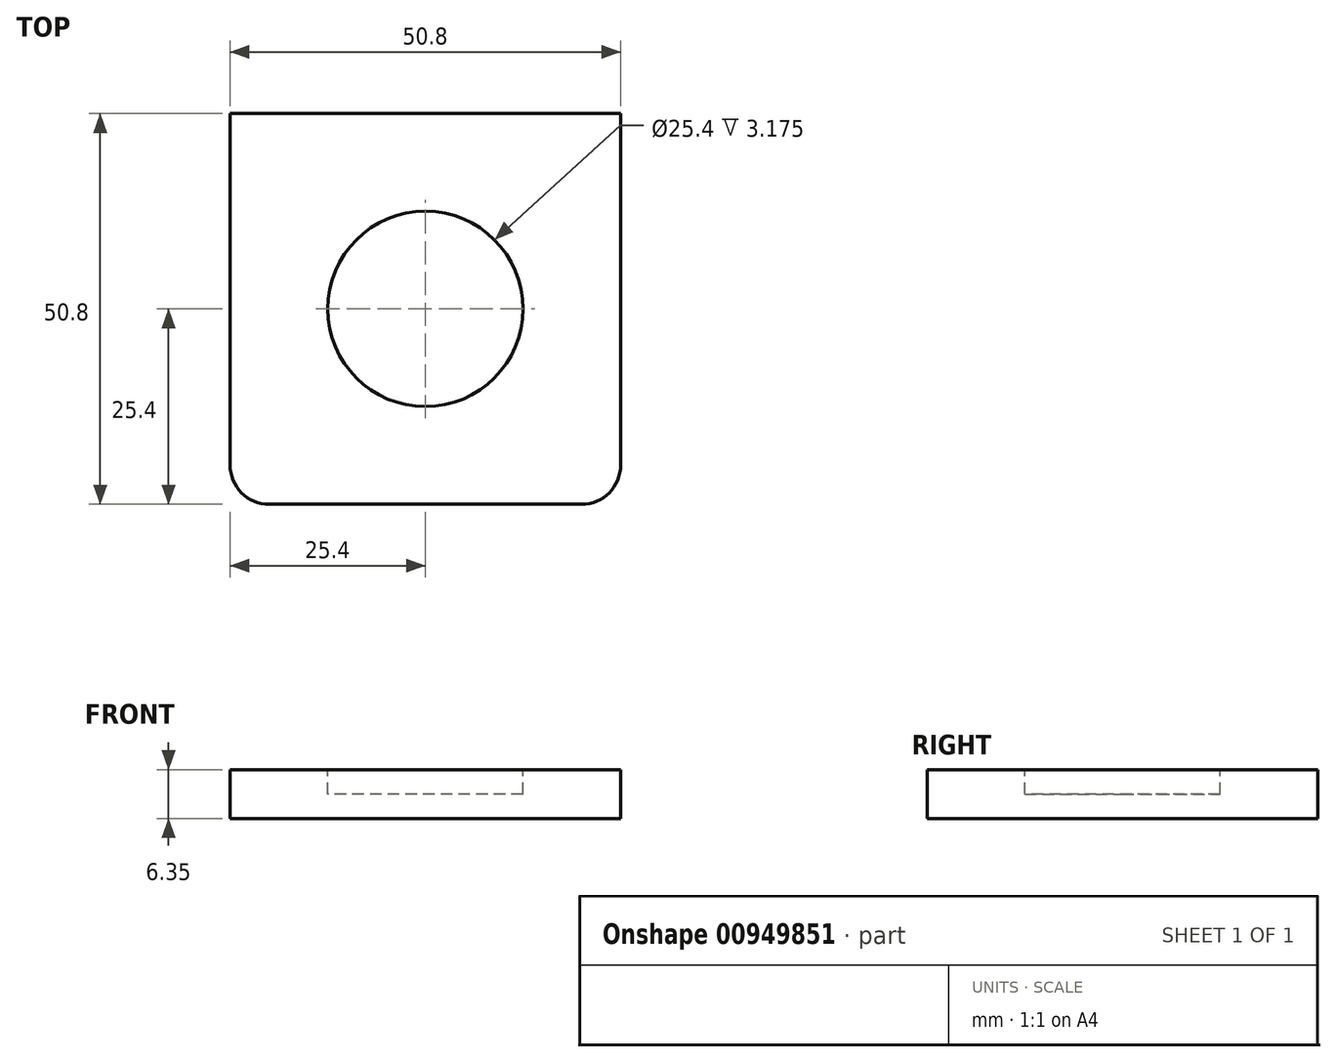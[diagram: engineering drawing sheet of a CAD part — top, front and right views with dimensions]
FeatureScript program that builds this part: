
annotation { "Feature Type Name" : "Feature", "Feature Type Description" : "" }
export const myFeature = defineFeature(function(context is Context, id is Id, definition is map)
    precondition{}
    {
        {
            var Q0;
            Q0=qCreatedBy(makeId("Top.planeOp"),FACE);
            var sketch = newSketch(context, id + "F0", { "sketchPlane" : qUnion([Q0])});
            skLineSegment(sketch, "E0.bottom", {"start": v(25.4, -25.4) * mm, "end": v(-25.4, -25.4) * mm});
            skLineSegment(sketch, "E0.top", {"start": v(25.4, 25.4) * mm, "end": v(-25.4, 25.4) * mm});
            skLineSegment(sketch, "E0.left", {"start": v(25.4, -25.4) * mm, "end": v(25.4, 25.4) * mm});
            skLineSegment(sketch, "E0.right", {"start": v(-25.4, -25.4) * mm, "end": v(-25.4, 25.4) * mm});
            skPoint(sketch, "E0.middle", {"position": v(0, 0) * mm});
            skSolve(sketch);
        }
        {
            var Q0;
            Q0=makeQuery(id+"F0.imprint","IMPRINT",FACE,{"disambiguationData":[TD([[makeQuery(id+"F0.imprint","IMPRINT",EDGE,{"derivedFrom":sQuery(id+"F0.wireOp",EDGE,"E0.bottom")}),-1.0]])]});
            extrude(context, id + "F1", {"entities" : qUnion([Q0]), "depth" : 6.35 * mm, "offsetDistance" : 25.4 * mm});
        }
        {
            var Q0;
            Q0=makeQuery(id+"F1.opExtrude","SWEPT_EDGE",EDGE,{"disambiguationData":[OSD([sQuery(id+"F0.wireOp",EDGE,"E0.bottom"),sQuery(id+"F0.wireOp",EDGE,"E0.right")])]});
            var Q1;
            Q1=makeQuery(id+"F1.opExtrude","SWEPT_EDGE",EDGE,{"disambiguationData":[OSD([sQuery(id+"F0.wireOp",EDGE,"E0.bottom"),sQuery(id+"F0.wireOp",EDGE,"E0.left")])]});
            fillet(context, id + "F2", {"entities" : qUnion([Q0, Q1]), "radius" : 5.08 * mm, "tangentPropagation" : true, "allowEdgeOverflow" : false});
        }
        {
            var Q0;
            Q0=makeQuery(id+"F1.opExtrude","CAP_FACE",FACE,{"disambiguationData":[OSD([sQuery(id+"F0.wireOp",EDGE,"E0.bottom"),sQuery(id+"F0.wireOp",EDGE,"E0.top"),sQuery(id+"F0.wireOp",EDGE,"E0.left"),sQuery(id+"F0.wireOp",EDGE,"E0.right")])],"isStart":false});
            var sketch = newSketch(context, id + "F3", { "sketchPlane" : qUnion([Q0])});
            skCircle(sketch, "E1", {"center": v(0, 0) * mm, "radius": 12.7 * mm});
            skSolve(sketch);
        }
        {
            var Q0;
            Q0=makeQuery(id+"F3.imprint","IMPRINT",FACE,{"disambiguationData":[TD([[makeQuery(id+"F3.imprint","IMPRINT",EDGE,{"derivedFrom":sQuery(id+"F3.wireOp",EDGE,"E1")}),1.0]])]});
            extrude(context, id + "F4", {"entities" : qUnion([Q0]), "operationType" : NewBodyOperationType.REMOVE, "oppositeDirection" : true, "depth" : 3.17 * mm, "offsetDistance" : 25.4 * mm});
        }
    });
